SOLIDWORKS PART (.sldprt)
format: sldprt  version: not decoded by parser v0  size: 198,656 bytes
history: native  units: mm
features: sketch x9, extrude x9, plane x3, material x1 (+13 scaffold rows collapsed)
feature tree (35):
  scaffold x13  (default folders/planes/origin — collapsed)
  material  "材质 <未指定>"
  plane  "前视基准面"
  plane  "上视基准面"
  plane  "右视基准面"
  sketch  "草图1"  dims[c1.D3=~4.38271mm c1.D1=4.0mm c1.D2=80.0mm c2.D1=40.0mm]
  extrude  "凸台-拉伸2"  Depth=1mm
  sketch  "草图2"
  extrude  "凸台-拉伸3"  Depth=1mm
  sketch  "草图3"  dims[D1=4.0mm D2=80.0mm D3=40.0mm]
  extrude  "凸台-拉伸4"  Depth=1mm
  sketch  "草图4"
  extrude  "凸台-拉伸5"  Depth=1mm
  sketch  "草图5"  dims[D1=4.0mm]
  extrude  "凸台-拉伸6"  Depth=1mm
  sketch  "草图6"
  extrude  "凸台-拉伸7"  Depth=1mm
  sketch  "草图7"
  extrude  "凸台-拉伸8"  Depth=1mm
  sketch  "草图8"  dims[D1=0.0mm D2=1.5mm D3=1.5mm D4=2.0mm]
  extrude  "凸台-拉伸9"  Depth=1mm
  sketch  "草图9"  dims[D1=0.0mm D2=1.5mm D3=1.5mm D4=2.0mm]
  extrude  "凸台-拉伸10"  Depth=1mm
decode coverage: 14 of 18 modeling features carry decoded parameters
note: ~ marks probable driven/reference dimensions
note: suppression state not decoded; provenance and decode notes live in map.json
